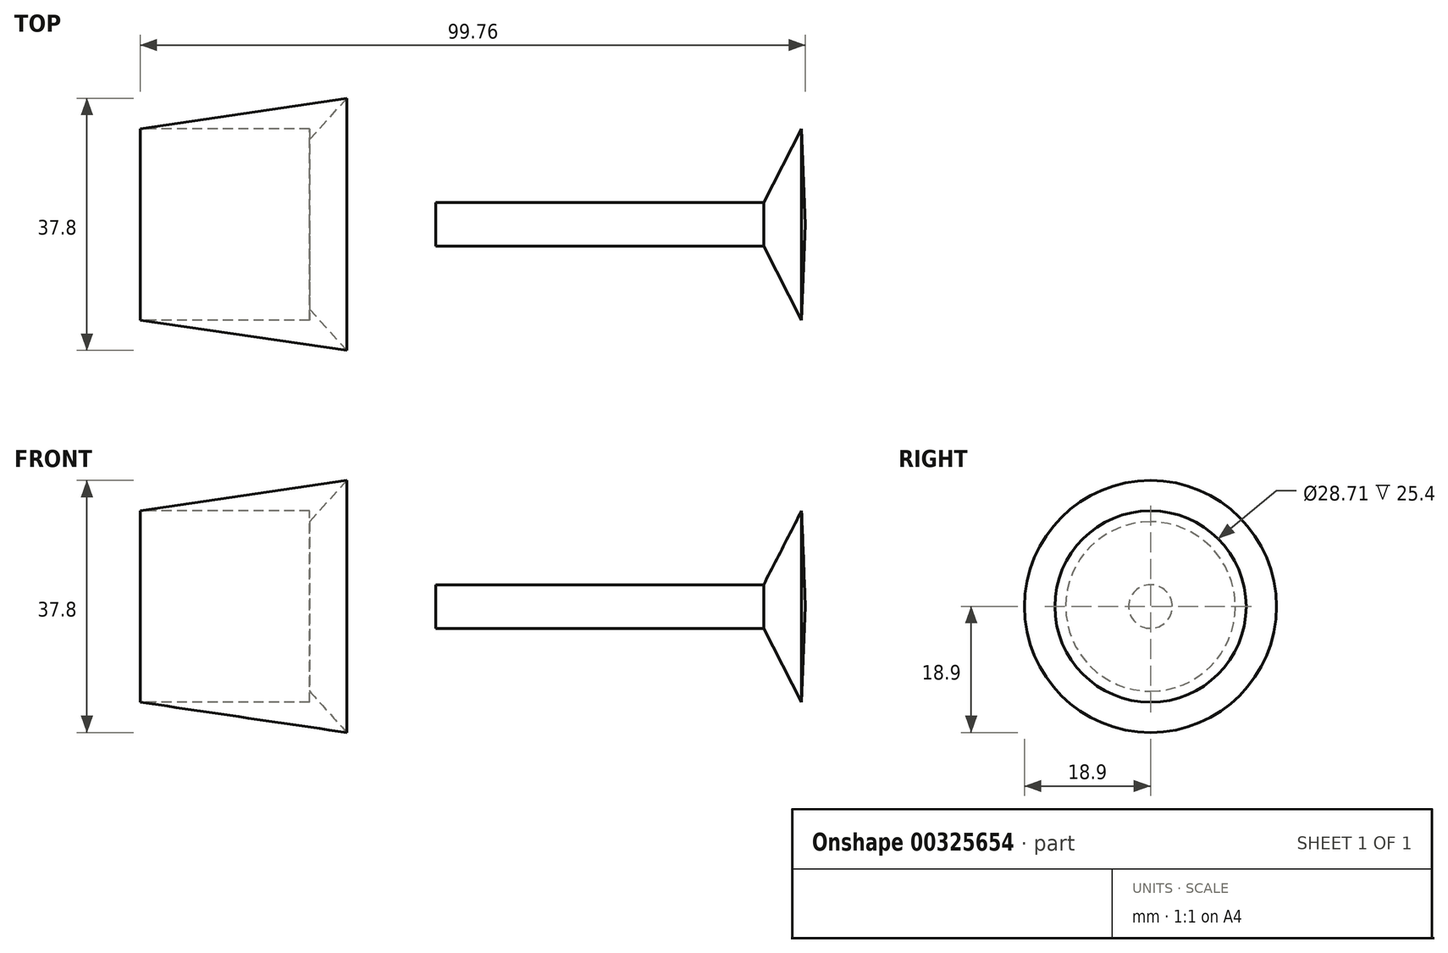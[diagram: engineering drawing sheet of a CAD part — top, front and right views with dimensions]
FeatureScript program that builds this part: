
annotation { "Feature Type Name" : "Feature", "Feature Type Description" : "" }
export const myFeature = defineFeature(function(context is Context, id is Id, definition is map)
    precondition{}
    {
        {
            var Q0;
            Q0=qCreatedBy(makeId("Front.planeOp"),FACE);
            var sketch = newSketch(context, id + "F0", { "sketchPlane" : qUnion([Q0])});
            skLineSegment(sketch, "E0", {"start": v(0, 0) * mm, "end": v(0, 14.35) * mm});
            skLineSegment(sketch, "E1", {"start": v(0, 14.35) * mm, "end": v(30.98, 18.9) * mm});
            skLineSegment(sketch, "E2", {"start": v(30.98, 18.9) * mm, "end": v(13.93, 0) * mm});
            skLineSegment(sketch, "E3", {"start": v(13.93, 0) * mm, "end": v(0, 0) * mm});
            skSolve(sketch);
        }
        {
            var Q0;
            Q0=makeQuery(id+"F0.imprint","IMPRINT",FACE,{"disambiguationData":[TD([[makeQuery(id+"F0.imprint","IMPRINT",EDGE,{"derivedFrom":sQuery(id+"F0.wireOp",EDGE,"E0")}),-1.0]])]});
            var Q1;
            Q1=sQuery(id+"F0.wireOp",EDGE,"E3");
            revolve(context, id + "F1", {"entities" : qUnion([Q0]), "axis" : qUnion([Q1]), "revolveType" : RevolveType.FULL});
        }
        {
            var Q0;
            Q0=makeQuery(id+"F1.opRevolve","SWEPT_FACE",FACE,{"disambiguationData":[OSD([sQuery(id+"F0.wireOp",EDGE,"E0")])]});
            var sketch = newSketch(context, id + "F2", { "sketchPlane" : qUnion([Q0])});
            skSolve(sketch);
        }
        {
            var Q0;
            Q0=makeQuery(id+"F2.imprint","IMPRINT",FACE,{"disambiguationData":[TD([[makeQuery(id+"F2.imprint","IMPRINT",EDGE,{"derivedFrom":makeQuery(id+"F1.opRevolve","SWEPT_EDGE",EDGE,{"disambiguationData":[OSD([sQuery(id+"F0.wireOp",EDGE,"E0"),sQuery(id+"F0.wireOp",EDGE,"E1")])]})}),-1.0]])]});
            extrude(context, id + "F3", {"entities" : qUnion([Q0]), "operationType" : NewBodyOperationType.REMOVE, "oppositeDirection" : true, "depth" : 25.4 * mm});
        }
        {
            var Q0;
            Q0=qCreatedBy(makeId("Front.planeOp"),FACE);
            var sketch = newSketch(context, id + "F4", { "sketchPlane" : qUnion([Q0])});
            skLineSegment(sketch, "E4.bottom", {"start": v(44.34, 0) * mm, "end": v(93.51, 0) * mm});
            skLineSegment(sketch, "E4.top", {"start": v(44.34, 3.27) * mm, "end": v(93.51, 3.27) * mm});
            skLineSegment(sketch, "E4.left", {"start": v(44.34, 0) * mm, "end": v(44.34, 3.27) * mm});
            skLineSegment(sketch, "E5", {"start": v(93.51, 3.27) * mm, "end": v(99.2, 14.35) * mm});
            skLineSegment(sketch, "E6", {"start": v(93.51, 0) * mm, "end": v(99.76, 0) * mm});
            skLineSegment(sketch, "E7", {"start": v(99.2, 14.35) * mm, "end": v(99.76, 0) * mm});
            skSolve(sketch);
        }
        {
            var Q0;
            Q0=makeQuery(id+"F4.imprint","IMPRINT",FACE,{"disambiguationData":[TD([[makeQuery(id+"F4.imprint","IMPRINT",EDGE,{"derivedFrom":sQuery(id+"F4.wireOp",EDGE,"E4.bottom")}),1.0]])]});
            var Q1;
            Q1=sQuery(id+"F4.wireOp",EDGE,"E4.bottom");
            revolve(context, id + "F5", {"entities" : qUnion([Q0]), "axis" : qUnion([Q1]), "revolveType" : RevolveType.FULL});
        }
    });
